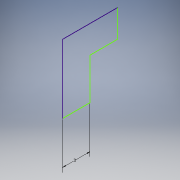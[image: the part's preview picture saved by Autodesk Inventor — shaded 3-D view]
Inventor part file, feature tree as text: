
AUTODESK INVENTOR PART (.ipt)
format: ipt  version: 2017 (Build 210142000, 142)  size: 84,480 bytes
history: native  units: mm
features: sketch x1
ambient origin geometry x8: Origin, YZ Plane, XZ Plane, XY Plane, X Axis, Y Axis, Z Axis, Center Point
feature tree (1):
  sketch  "Sketch1"  dims[d0=3.0mm]
